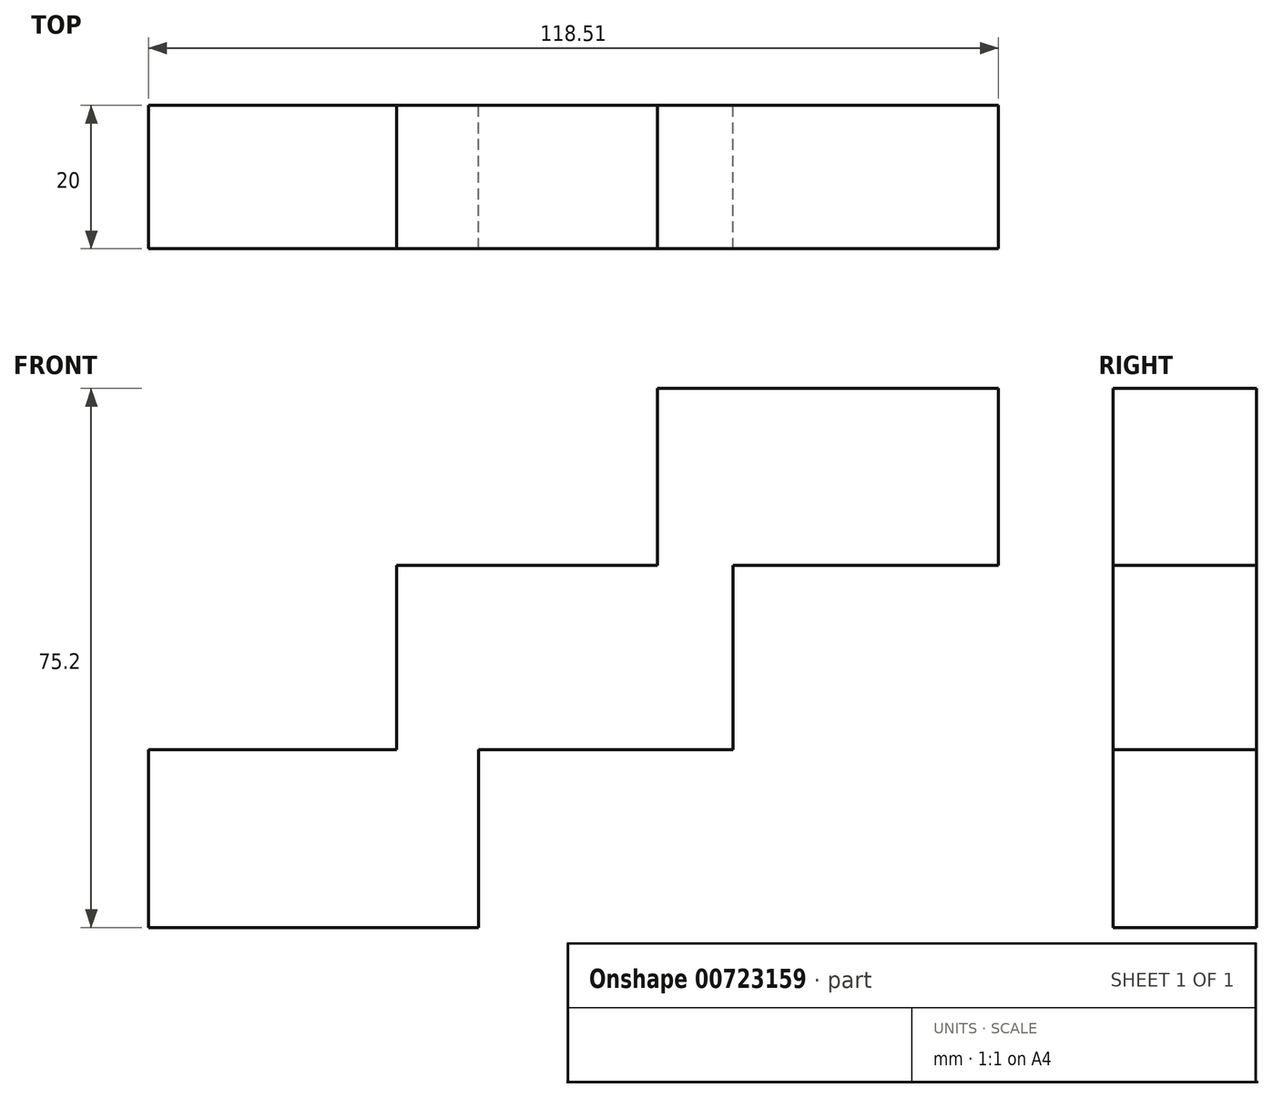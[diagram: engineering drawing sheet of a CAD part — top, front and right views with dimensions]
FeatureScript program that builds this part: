
annotation { "Feature Type Name" : "Feature", "Feature Type Description" : "" }
export const myFeature = defineFeature(function(context is Context, id is Id, definition is map)
    precondition{}
    {
        {
            var Q0;
            Q0=qCreatedBy(makeId("Front.planeOp"),FACE);
            var sketch = newSketch(context, id + "F0", { "sketchPlane" : qUnion([Q0])});
            skLineSegment(sketch, "E0", {"start": v(13.39, 50.38) * mm, "end": v(60.9, 50.38) * mm});
            skLineSegment(sketch, "E1", {"start": v(60.9, 25.72) * mm, "end": v(60.9, 50.38) * mm});
            skLineSegment(sketch, "E2", {"start": v(60.9, 25.72) * mm, "end": v(23.91, 25.72) * mm});
            skLineSegment(sketch, "E3", {"start": v(23.91, 25.72) * mm, "end": v(23.91, 0) * mm});
            skLineSegment(sketch, "E4", {"start": v(23.91, 0) * mm, "end": v(-11.58, 0) * mm});
            skLineSegment(sketch, "E5", {"start": v(-11.58, 0) * mm, "end": v(-11.58, -24.82) * mm});
            skLineSegment(sketch, "E6", {"start": v(-11.58, -24.82) * mm, "end": v(-57.6, -24.82) * mm});
            skLineSegment(sketch, "E7", {"start": v(-57.6, -24.82) * mm, "end": v(-57.6, 0) * mm});
            skLineSegment(sketch, "E8", {"start": v(-57.6, 0) * mm, "end": v(-23.01, 0) * mm});
            skLineSegment(sketch, "E9", {"start": v(-23.01, 0) * mm, "end": v(-23.01, 25.72) * mm});
            skLineSegment(sketch, "E10", {"start": v(-23.01, 25.72) * mm, "end": v(13.39, 25.72) * mm});
            skLineSegment(sketch, "E11", {"start": v(13.39, 25.72) * mm, "end": v(13.39, 50.38) * mm});
            skSolve(sketch);
        }
        {
            var Q0;
            Q0=makeQuery(id+"F0.imprint","IMPRINT",FACE,{"disambiguationData":[TD([[makeQuery(id+"F0.imprint","IMPRINT",EDGE,{"derivedFrom":sQuery(id+"F0.wireOp",EDGE,"E0")}),-1.0]])]});
            extrude(context, id + "F1", {"entities" : qUnion([Q0]), "depth" : 20 * mm, "offsetDistance" : 25.4 * mm});
        }
    });
